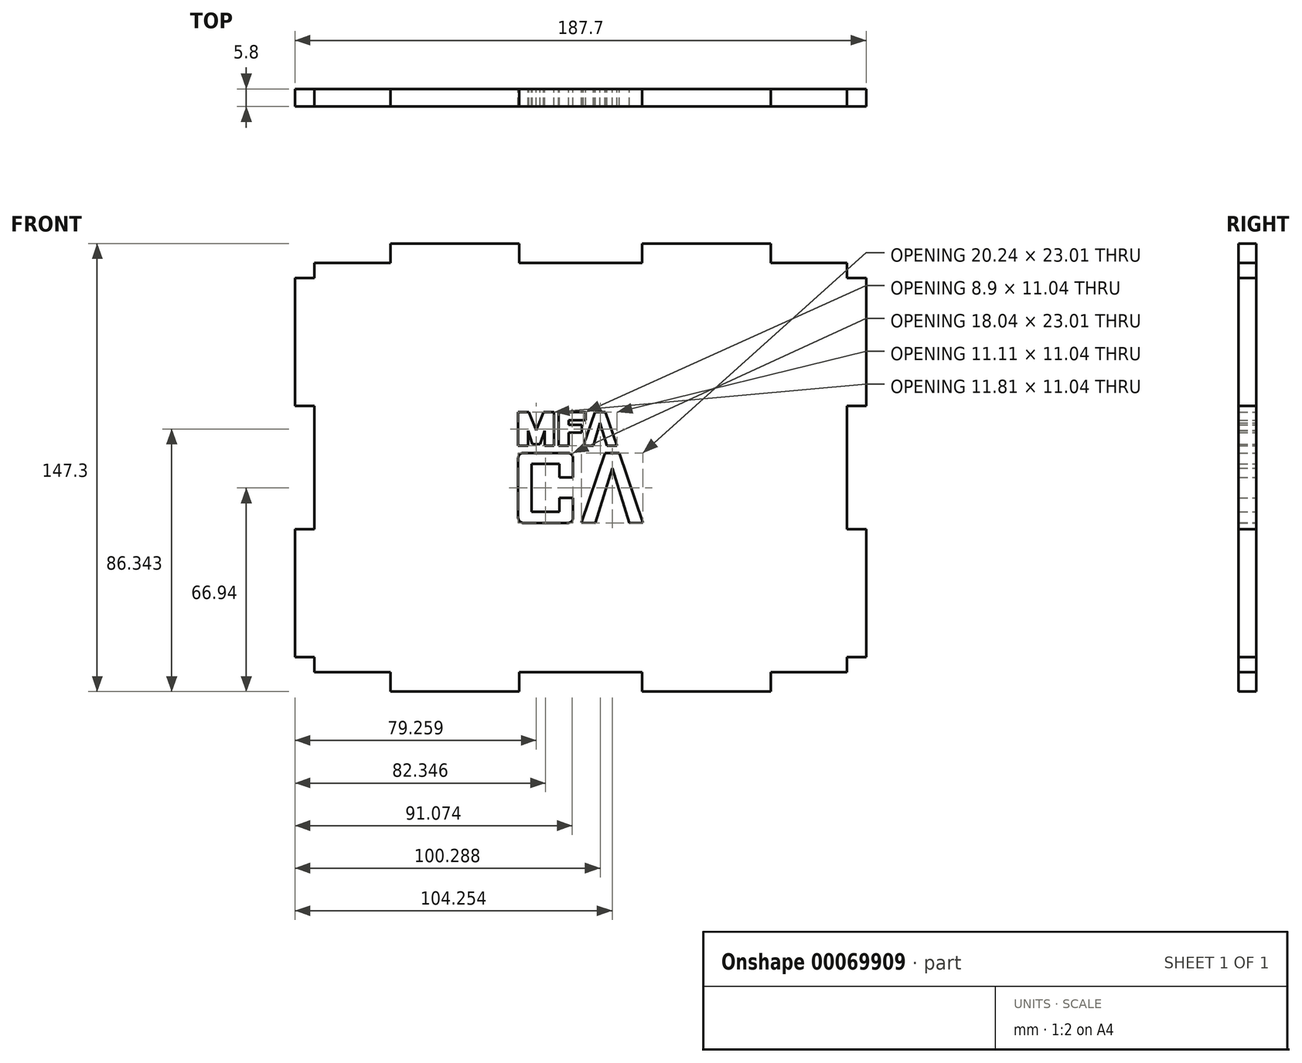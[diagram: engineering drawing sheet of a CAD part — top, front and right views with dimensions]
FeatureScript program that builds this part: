
annotation { "Feature Type Name" : "Feature", "Feature Type Description" : "" }
export const myFeature = defineFeature(function(context is Context, id is Id, definition is map)
    precondition{}
    {
        {
            var Q0;
            Q0=qCreatedBy(makeId("Front.planeOp"),FACE);
            var sketch = newSketch(context, id + "F0", { "sketchPlane" : qUnion([Q0])});
            skLineSegment(sketch, "E0.bottom", {"start": v(87.5, 67.3) * mm, "end": v(62.5, 67.3) * mm});
            skLineSegment(sketch, "E0.top", {"start": v(87.5, -67.3) * mm, "end": v(62.5, -67.3) * mm});
            skLineSegment(sketch, "E0.left", {"start": v(87.5, 67.3) * mm, "end": v(87.5, 62.3) * mm});
            skLineSegment(sketch, "E0.right", {"start": v(-87.5, 67.3) * mm, "end": v(-87.5, 62.3) * mm});
            skPoint(sketch, "E0.middle", {"position": v(0, 0) * mm});
            skLineSegment(sketch, "E1.top", {"start": v(-62.5, 73.65) * mm, "end": v(-20.2, 73.65) * mm});
            skLineSegment(sketch, "E1.left", {"start": v(-62.5, 67.3) * mm, "end": v(-62.5, 73.65) * mm});
            skLineSegment(sketch, "E1.right", {"start": v(-20.2, 67.3) * mm, "end": v(-20.2, 73.65) * mm});
            skLineSegment(sketch, "E2.top", {"start": v(20.2, 73.65) * mm, "end": v(62.5, 73.65) * mm});
            skLineSegment(sketch, "E2.left", {"start": v(20.2, 67.3) * mm, "end": v(20.2, 73.65) * mm});
            skLineSegment(sketch, "E2.right", {"start": v(62.5, 67.3) * mm, "end": v(62.5, 73.65) * mm});
            skLineSegment(sketch, "E3.trimOffspring", {"start": v(-62.5, 67.3) * mm, "end": v(-87.5, 67.3) * mm});
            skLineSegment(sketch, "E4.trimOffspring", {"start": v(20.2, 67.3) * mm, "end": v(-20.2, 67.3) * mm});
            skLineSegment(sketch, "E5.top", {"start": v(-62.5, -73.65) * mm, "end": v(-20.2, -73.65) * mm});
            skLineSegment(sketch, "E5.left", {"start": v(-62.5, -67.3) * mm, "end": v(-62.5, -73.65) * mm});
            skLineSegment(sketch, "E5.right", {"start": v(-20.2, -67.3) * mm, "end": v(-20.2, -73.65) * mm});
            skLineSegment(sketch, "E6.top", {"start": v(20.2, -73.65) * mm, "end": v(62.5, -73.65) * mm});
            skLineSegment(sketch, "E6.left", {"start": v(20.2, -67.3) * mm, "end": v(20.2, -73.65) * mm});
            skLineSegment(sketch, "E6.right", {"start": v(62.5, -67.3) * mm, "end": v(62.5, -73.65) * mm});
            skLineSegment(sketch, "E7.trimOffspring", {"start": v(-62.5, -67.3) * mm, "end": v(-87.5, -67.3) * mm});
            skLineSegment(sketch, "E8.trimOffspring", {"start": v(20.2, -67.3) * mm, "end": v(-20.2, -67.3) * mm});
            skLineSegment(sketch, "E9.bottom", {"start": v(87.5, -62.3) * mm, "end": v(93.85, -62.3) * mm});
            skLineSegment(sketch, "E9.top", {"start": v(87.5, -20.3) * mm, "end": v(93.85, -20.3) * mm});
            skLineSegment(sketch, "E9.right", {"start": v(93.85, -62.3) * mm, "end": v(93.85, -20.3) * mm});
            skLineSegment(sketch, "E10.bottom", {"start": v(87.5, 20.3) * mm, "end": v(93.85, 20.3) * mm});
            skLineSegment(sketch, "E10.top", {"start": v(87.5, 62.3) * mm, "end": v(93.85, 62.3) * mm});
            skLineSegment(sketch, "E10.right", {"start": v(93.85, 20.3) * mm, "end": v(93.85, 62.3) * mm});
            skLineSegment(sketch, "E11.bottom", {"start": v(-87.5, 62.3) * mm, "end": v(-93.85, 62.3) * mm});
            skLineSegment(sketch, "E11.top", {"start": v(-87.5, 20.3) * mm, "end": v(-93.85, 20.3) * mm});
            skLineSegment(sketch, "E11.right", {"start": v(-93.85, 62.3) * mm, "end": v(-93.85, 20.3) * mm});
            skLineSegment(sketch, "E12.bottom", {"start": v(-87.5, -20.3) * mm, "end": v(-93.85, -20.3) * mm});
            skLineSegment(sketch, "E12.top", {"start": v(-87.5, -62.3) * mm, "end": v(-93.85, -62.3) * mm});
            skLineSegment(sketch, "E12.right", {"start": v(-93.85, -20.3) * mm, "end": v(-93.85, -62.3) * mm});
            skLineSegment(sketch, "E13.trimOffspring", {"start": v(87.5, 20.3) * mm, "end": v(87.5, -20.3) * mm});
            skLineSegment(sketch, "E14.trimOffspring", {"start": v(87.5, -62.3) * mm, "end": v(87.5, -67.3) * mm});
            skLineSegment(sketch, "E15.trimOffspring", {"start": v(-87.5, 20.3) * mm, "end": v(-87.5, -20.3) * mm});
            skLineSegment(sketch, "E16.trimOffspring", {"start": v(-87.5, -62.3) * mm, "end": v(-87.5, -67.3) * mm});
            skLineSegment(sketch, "E17", {"start": v(-4.28, -18.21) * mm, "end": v(-18.72, -18.21) * mm});
            skLineSegment(sketch, "E18", {"start": v(-20.52, -16.41) * mm, "end": v(-20.52, 3) * mm});
            skLineSegment(sketch, "E19", {"start": v(-18.72, 4.8) * mm, "end": v(-4.28, 4.8) * mm});
            skLineSegment(sketch, "E20", {"start": v(-2.48, 3) * mm, "end": v(-2.48, -3.19) * mm});
            skLineSegment(sketch, "E21", {"start": v(-2.48, -3.19) * mm, "end": v(-6.91, -3.19) * mm});
            skLineSegment(sketch, "E22", {"start": v(-6.91, -3.19) * mm, "end": v(-6.91, 1.15) * mm});
            skLineSegment(sketch, "E23", {"start": v(-6.91, 1.15) * mm, "end": v(-16.1, 1.15) * mm});
            skLineSegment(sketch, "E24", {"start": v(-16.1, 1.15) * mm, "end": v(-16.1, -14.57) * mm});
            skLineSegment(sketch, "E25", {"start": v(-16.1, -14.57) * mm, "end": v(-6.91, -14.57) * mm});
            skLineSegment(sketch, "E26", {"start": v(-6.91, -14.57) * mm, "end": v(-6.91, -9.96) * mm});
            skLineSegment(sketch, "E27", {"start": v(-6.91, -9.96) * mm, "end": v(-2.48, -9.96) * mm});
            skLineSegment(sketch, "E28", {"start": v(-2.48, -9.96) * mm, "end": v(-2.48, -16.41) * mm});
            skLineSegment(sketch, "E29", {"start": v(0.29, -18.15) * mm, "end": v(8.06, 4.8) * mm});
            skLineSegment(sketch, "E30", {"start": v(8.06, 4.8) * mm, "end": v(12.75, 4.8) * mm});
            skLineSegment(sketch, "E31", {"start": v(12.75, 4.8) * mm, "end": v(20.52, -18.15) * mm});
            skLineSegment(sketch, "E32", {"start": v(20.52, -18.15) * mm, "end": v(15.98, -18.21) * mm});
            skLineSegment(sketch, "E33", {"start": v(15.98, -18.21) * mm, "end": v(10.37, -0.24) * mm});
            skLineSegment(sketch, "E34", {"start": v(10.37, -0.24) * mm, "end": v(4.8, -18.21) * mm});
            skLineSegment(sketch, "E35", {"start": v(4.8, -18.21) * mm, "end": v(0.29, -18.15) * mm});
            skLineSegment(sketch, "E36", {"start": v(-20.5, 7.17) * mm, "end": v(-17.29, 7.17) * mm});
            skLineSegment(sketch, "E37", {"start": v(-17.29, 7.17) * mm, "end": v(-17.29, 12.1) * mm});
            skLineSegment(sketch, "E38", {"start": v(-17.29, 12.1) * mm, "end": v(-15.88, 7.65) * mm});
            skLineSegment(sketch, "E39", {"start": v(-15.88, 7.65) * mm, "end": v(-13.25, 7.65) * mm});
            skLineSegment(sketch, "E40", {"start": v(-13.25, 7.65) * mm, "end": v(-11.85, 12.1) * mm});
            skLineSegment(sketch, "E41", {"start": v(-11.85, 12.1) * mm, "end": v(-11.85, 7.17) * mm});
            skLineSegment(sketch, "E42", {"start": v(-11.85, 7.17) * mm, "end": v(-8.69, 7.17) * mm});
            skLineSegment(sketch, "E43", {"start": v(-8.69, 7.17) * mm, "end": v(-8.69, 18.21) * mm});
            skLineSegment(sketch, "E44", {"start": v(-8.69, 18.21) * mm, "end": v(-12.13, 18.21) * mm});
            skLineSegment(sketch, "E45", {"start": v(-12.13, 18.21) * mm, "end": v(-14.54, 12.29) * mm});
            skLineSegment(sketch, "E46", {"start": v(-14.54, 12.29) * mm, "end": v(-17.03, 18.21) * mm});
            skLineSegment(sketch, "E47", {"start": v(-17.03, 18.21) * mm, "end": v(-20.5, 18.21) * mm});
            skLineSegment(sketch, "E48", {"start": v(-20.5, 18.21) * mm, "end": v(-20.5, 7.17) * mm});
            skLineSegment(sketch, "E49", {"start": v(-3.96, 7.17) * mm, "end": v(-7.23, 7.17) * mm});
            skLineSegment(sketch, "E50", {"start": v(-7.23, 7.17) * mm, "end": v(-7.23, 18.21) * mm});
            skLineSegment(sketch, "E51", {"start": v(-7.23, 18.21) * mm, "end": v(1.68, 18.21) * mm});
            skLineSegment(sketch, "E52", {"start": v(1.68, 18.21) * mm, "end": v(1.68, 15.55) * mm});
            skLineSegment(sketch, "E53", {"start": v(1.68, 15.55) * mm, "end": v(-3.96, 15.55) * mm});
            skLineSegment(sketch, "E54", {"start": v(-3.96, 15.55) * mm, "end": v(-3.96, 14.05) * mm});
            skLineSegment(sketch, "E55", {"start": v(-3.96, 14.05) * mm, "end": v(0.4, 14.05) * mm});
            skLineSegment(sketch, "E56", {"start": v(0.4, 14.05) * mm, "end": v(0.4, 11.54) * mm});
            skLineSegment(sketch, "E57", {"start": v(0.4, 11.54) * mm, "end": v(-3.96, 11.54) * mm});
            skLineSegment(sketch, "E58", {"start": v(-3.96, 11.54) * mm, "end": v(-3.96, 7.17) * mm});
            skLineSegment(sketch, "E59", {"start": v(0.88, 7.2) * mm, "end": v(4.2, 7.17) * mm});
            skLineSegment(sketch, "E60", {"start": v(4.2, 7.17) * mm, "end": v(6.43, 14.69) * mm});
            skLineSegment(sketch, "E61", {"start": v(6.43, 14.69) * mm, "end": v(8.64, 7.17) * mm});
            skLineSegment(sketch, "E62", {"start": v(8.64, 7.17) * mm, "end": v(12, 7.2) * mm});
            skLineSegment(sketch, "E63", {"start": v(12, 7.2) * mm, "end": v(8.18, 18.21) * mm});
            skLineSegment(sketch, "E64", {"start": v(8.18, 18.21) * mm, "end": v(4.7, 18.21) * mm});
            skLineSegment(sketch, "E65", {"start": v(4.7, 18.21) * mm, "end": v(0.88, 7.2) * mm});
            skPoint(sketch, "E66.visualSharp", {"position": v(-2.48, 4.8) * mm});
            skArc(sketch, "E66.filletArc", {"start": v(-2.48, 3) * mm, "mid": v(-3.01, 4.27) * mm, "end": v(-4.28, 4.8) * mm});
            skPoint(sketch, "E67.visualSharp", {"position": v(-20.52, 4.8) * mm});
            skArc(sketch, "E67.filletArc", {"start": v(-18.72, 4.8) * mm, "mid": v(-20, 4.27) * mm, "end": v(-20.52, 3) * mm});
            skPoint(sketch, "E68.visualSharp", {"position": v(-20.52, -18.21) * mm});
            skArc(sketch, "E68.filletArc", {"start": v(-20.52, -16.41) * mm, "mid": v(-20, -17.69) * mm, "end": v(-18.72, -18.21) * mm});
            skPoint(sketch, "E69.visualSharp", {"position": v(-2.48, -18.21) * mm});
            skArc(sketch, "E69.filletArc", {"start": v(-4.28, -18.21) * mm, "mid": v(-3.01, -17.69) * mm, "end": v(-2.48, -16.41) * mm});
            skSolve(sketch);
        }
        {
            var Q0;
            Q0=makeQuery(id+"F0.imprint","IMPRINT",FACE,{"disambiguationData":[TD([[makeQuery(id+"F0.imprint","IMPRINT",EDGE,{"derivedFrom":sQuery(id+"F0.wireOp",EDGE,"E0.bottom")}),1.0]])]});
            extrude(context, id + "F1", {"entities" : qUnion([Q0]), "depth" : 5.8 * mm});
        }
    });
